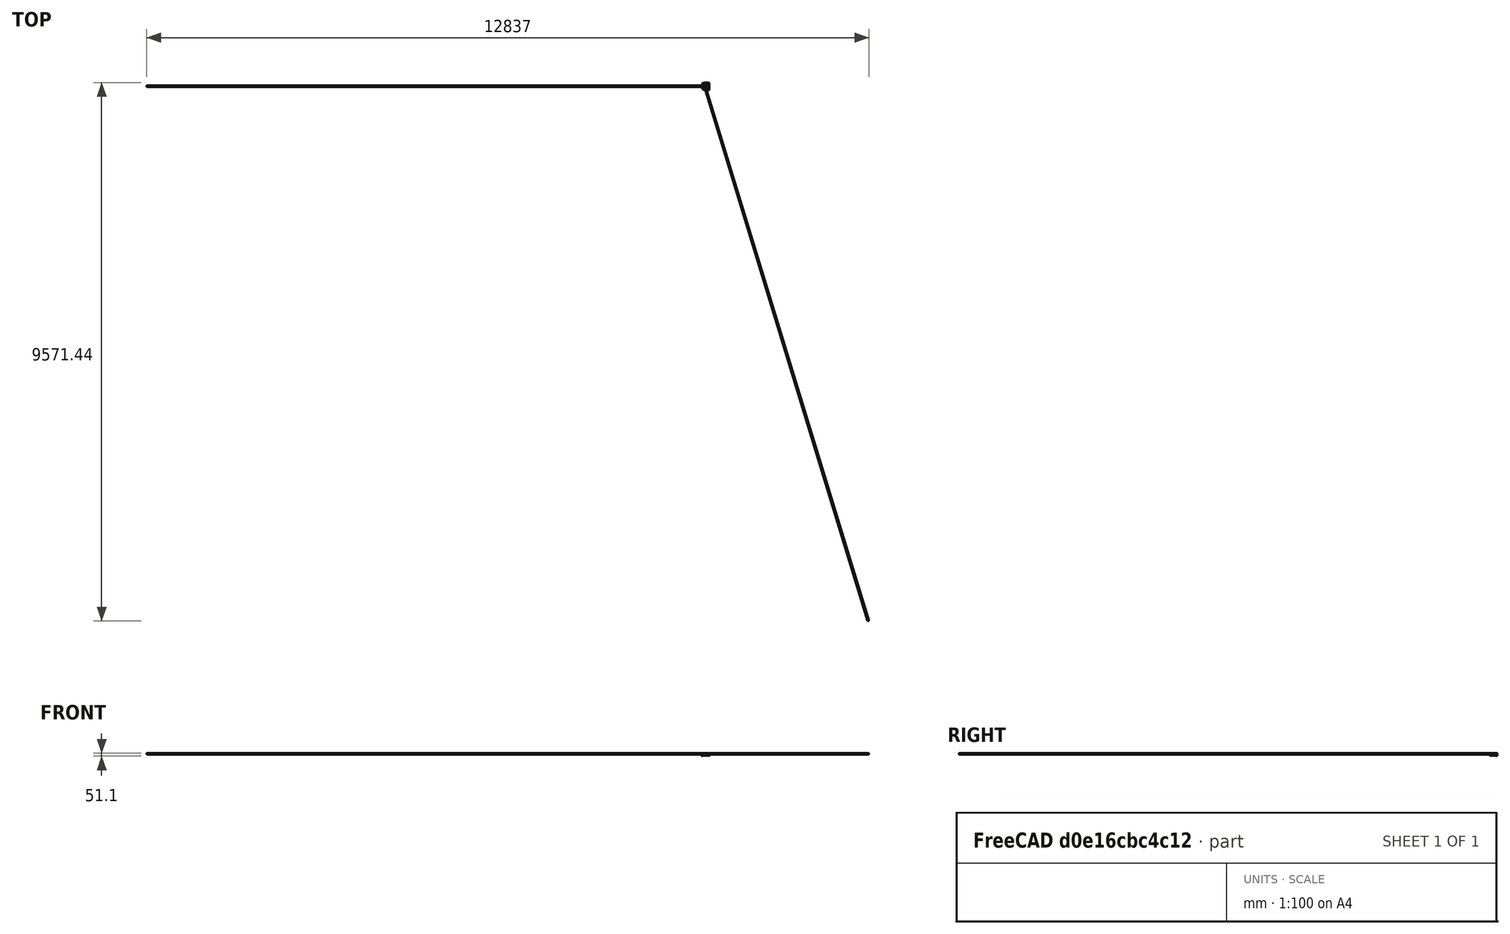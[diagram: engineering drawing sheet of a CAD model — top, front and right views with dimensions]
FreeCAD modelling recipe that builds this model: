
FCSTD DOCUMENT  (FreeCAD 0.16R)
Label: chainguard25TRearRev4
License: All rights reserved
LicenseURL: http://en.wikipedia.org/wiki/All_rights_reserved
objects: Sketcher::SketchObject×12, PartDesign::Pocket×6, PartDesign::Pad×5, PartDesign::Fillet×5, Part::FeaturePython×4, Mesh::Feature×4
note: 43 computed .brp shape members not serialized (recipe doc carries the construction recipe); baked Part::Feature solids carry a one-line shape summary decoded from their .brp

FEATURE [Sketcher::SketchObject] Sketch001
  sketch-geometry (7):
    g0: LineSegment StartX=60 StartY=64 StartZ=0 EndX=0 EndY=64 EndZ=0
    g1: LineSegment StartX=60 StartY=-64 StartZ=0 EndX=0 EndY=-64 EndZ=0
    g2: ArcOfCircle CenterX=8.21903e-05 CenterY=0 CenterZ=0 NormalX=0 NormalY=0 NormalZ=1 Radius=64 StartAngle=1.5708 EndAngle=4.71239
    g3: Circle CenterX=0 CenterY=0 CenterZ=0 NormalX=0 NormalY=0 NormalZ=1 Radius=45
    g4: ArcOfCircle CenterX=60 CenterY=51 CenterZ=0 NormalX=0 NormalY=0 NormalZ=1 Radius=13 StartAngle=0 EndAngle=1.5708
    g5: ArcOfCircle CenterX=60 CenterY=-51 CenterZ=0 NormalX=0 NormalY=0 NormalZ=1 Radius=13 StartAngle=4.71239 EndAngle=6.28319
    g6: LineSegment StartX=73 StartY=51 StartZ=0 EndX=73 EndY=-51 EndZ=0
  constraints (23):
    c: Horizontal(g0)
    c: Horizontal(g1)
    c: Coincident(g2,g1)
    c: Coincident(g0,g2)
    c: DistanceX(g1,g0) = 0
    c: Equal(g0,g1)
    c: DistanceY(g1,g0) = 128
    c: Radius(g2) = 64
    c: Symmetric(g1,g0,g-1)
    c: Radius(g3) = 45
    c: Coincident(g3,g-1)
    c: PointOnObject(g4,g0)
    c: Radius(g4) = 13
    c: DistanceX(g0,g0) = 60
    c: Equal(g5,g4)
    c: Vertical(g6)
    c: DistanceX(g-1,g6) = 73
    c: Symmetric(g6,g6,g-1)
    c: DistanceY(g6,g6) = 102
    c: Coincident(g4,g6)
    c: Coincident(g5,g6)
    c: Coincident(g1,g5)
    c: Coincident(g0,g4)
FEATURE [PartDesign::Pad] Pad  label="Faceplate"
  Length = 1.12
  Length2 = 100
  Reversed = true
  Sketch = -> Sketch001
  Type = 0
FEATURE [Sketcher::SketchObject] Sketch002
  sketch-geometry (8):
    g0: LineSegment StartX=60 StartY=64 StartZ=0 EndX=0 EndY=64 EndZ=0
    g1: LineSegment StartX=60 StartY=-64 StartZ=0 EndX=0 EndY=-64 EndZ=0
    g2: ArcOfCircle CenterX=6.44712e-05 CenterY=0 CenterZ=0 NormalX=0 NormalY=0 NormalZ=1 Radius=64 StartAngle=1.5708 EndAngle=4.71239
    g3: LineSegment StartX=0 StartY=62 StartZ=0 EndX=60 EndY=62 EndZ=0
    g4: LineSegment StartX=0 StartY=-62 StartZ=0 EndX=60 EndY=-62 EndZ=0
    g5: LineSegment StartX=60 StartY=64 StartZ=0 EndX=60 EndY=62 EndZ=0
    g6: LineSegment StartX=60 StartY=-62 StartZ=0 EndX=60 EndY=-64 EndZ=0
    g7: ArcOfCircle CenterX=1.45954e-05 CenterY=0 CenterZ=0 NormalX=0 NormalY=0 NormalZ=1 Radius=62 StartAngle=1.5708 EndAngle=4.71239
  constraints (25):
    c: Horizontal(g0)
    c: Horizontal(g1)
    c: Coincident(g2,g1)
    c: Coincident(g0,g2)
    c: DistanceX(g1,g0) = 0
    c: Equal(g0,g1)
    c: DistanceY(g1,g0) = 128
    c: Radius(g2) = 64
    c: Symmetric(g1,g0,g-1)
    c: Radius(g7) = 62
    c: Parallel(g0,g3)
    c: DistanceY(g3,g0) = 2
    c: DistanceY(g1,g4) = 2
    c: Parallel(g4,g1)
    c: DistanceX(g0,g3) = 0
    c: DistanceX(g4) = 0
    c: DistanceX(g0) = 60
    c: Equal(g3,g0)
    c: Equal(g4,g0)
    c: Coincident(g4,g6)
    c: Coincident(g6,g1)
    c: Coincident(g5,g3)
    c: Coincident(g5,g0)
    c: Coincident(g7,g3)
    c: Coincident(g7,g4)
FEATURE [PartDesign::Pad] Pad001  label="Connector"
  Length = 12
  Length2 = 100
  Sketch = -> Sketch002
  Type = 0
FEATURE [Sketcher::SketchObject] Sketch017
  sketch-geometry (5):
    g0: LineSegment [constr] StartX=-6 StartY=2 StartZ=0 EndX=-29.8283 EndY=79.9388 EndZ=0
    g1: LineSegment StartX=-7.74339 StartY=67.5577 StartZ=0 EndX=-41.2141 EndY=57.3247 EndZ=0
    g2: LineSegment StartX=-41.2141 StartY=57.3247 StartZ=0 EndX=-39.4598 EndY=51.5868 EndZ=0
    g3: LineSegment StartX=-39.4598 StartY=51.5868 StartZ=0 EndX=-5.98916 EndY=61.8199 EndZ=0
    g4: LineSegment StartX=-5.98916 StartY=61.8199 StartZ=0 EndX=-7.74339 EndY=67.5577 EndZ=0
  constraints (15):
    c: DistanceY(g-1,g0) = 2
    c: DistanceX(g-1,g0) = -6
    c: Angle(g0) = 1.8675
    c: Coincident(g1,g2)
    c: Coincident(g2,g3)
    c: Coincident(g3,g4)
    c: Coincident(g1,g4)
    c: Parallel(g2,g4)
    c: Parallel(g1,g3)
    c: Perpendicular(g2,g1)
    c: Distance(g4) = 6
    c: Distance(g1) = 35
    c: Symmetric(g3,g2,g0)
    c: Distance(g-1,g1) = 68
    c: Distance(g0) = 81.5
FEATURE [Sketcher::SketchObject] Sketch020
  sketch-geometry (4):
    g0: LineSegment StartX=67 StartY=35 StartZ=0 EndX=73 EndY=35 EndZ=0
    g1: LineSegment StartX=73 StartY=35 StartZ=0 EndX=73 EndY=-25 EndZ=0
    g2: LineSegment StartX=73 StartY=-25 StartZ=0 EndX=67 EndY=-25 EndZ=0
    g3: LineSegment StartX=67 StartY=-25 StartZ=0 EndX=67 EndY=35 EndZ=0
  constraints (12):
    c: Coincident(g0,g1)
    c: Coincident(g1,g2)
    c: Coincident(g2,g3)
    c: Coincident(g3,g0)
    c: Horizontal(g0)
    c: Horizontal(g2)
    c: Vertical(g1)
    c: Vertical(g3)
    c: DistanceX(g-1,g0) = 73
    c: DistanceX(g0,g0) = 6
    c: DistanceY(g-1,g0) = 35
    c: DistanceY(g1,g1) = 60
FEATURE [PartDesign::Pad] Pad004  label="SyncBoss"
  Length = 31
  Length2 = 100
  Sketch = -> Sketch020
  Type = 0
FEATURE [Sketcher::SketchObject] Sketch021
  ExternalGeometry = -> [Pad004]
  Placement = pos=(73,0,0) rot=(0.57735,0.57735,0.57735;2.0944rad)
  Support = -> Pad004 [Face2]
  sketch-geometry (1):
    g0: Circle CenterX=5 CenterY=31 CenterZ=0 NormalX=0 NormalY=0 NormalZ=1 Radius=11.2
  constraints (2):
    c: Symmetric(g-4,g-3,g0)
    c: Radius(g0) = 11.2
FEATURE [PartDesign::Pocket] Pocket  label="SyncHole"
  Length = 5
  Sketch = -> Sketch021
  Type = 1
FEATURE [PartDesign::Pad] Pad005  label="STBoss"
  Length = 32
  Length2 = 1
  Sketch = -> Sketch017
  Type = 4
FEATURE [Sketcher::SketchObject] Sketch022
  ExternalGeometry = -> [Pad005]
  Placement = pos=(-19.5508,63.9478,0) rot=(-0.105093,0.703191,0.703191;3.35101rad)
  Support = -> Pad005 [Face1]
  sketch-geometry (1):
    g0: Circle CenterX=5.15309 CenterY=32 CenterZ=0 NormalX=0 NormalY=0 NormalZ=1 Radius=11.2
  constraints (2):
    c: Symmetric(g-4,g-3,g0)
    c: Radius(g0) = 11.2
FEATURE [PartDesign::Pocket] Pocket006  label="SThole"
  Length = 5
  Sketch = -> Sketch022
  Type = 1
FEATURE [Sketcher::SketchObject] Sketch023
  Placement = pos=(-19.5508,63.9478,0) rot=(-0.105093,0.703191,0.703191;3.35101rad)
  Support = -> Pocket006 [Face1]
  sketch-geometry (3):
    g0: LineSegment StartX=31.754 StartY=21.6568 StartZ=0 EndX=10.7035 EndY=-1 EndZ=0
    g1: LineSegment StartX=10.7035 StartY=-1 StartZ=0 EndX=40.8501 EndY=-7.90189 EndZ=0
    g2: LineSegment StartX=40.8501 StartY=-7.90189 StartZ=0 EndX=31.754 EndY=21.6568 EndZ=0
  constraints (9):
    c: Coincident(g0,g1)
    c: Coincident(g1,g2)
    c: Coincident(g0,g2)
    c: Equal(g0,g2)
    c: Equal(g2,g1)
    c: DistanceY(g0,g-1) = 1
    c: Angle(g1) = -0.225065
    c: Distance(g2) = 30.9266
    c: DistanceX(g-1,g0) = 10.7035
FEATURE [PartDesign::Pocket] Pocket007  label="STbevel1"
  Length = 6
  Sketch = -> Sketch023
  Type = 0
FEATURE [Sketcher::SketchObject] Sketch024
  sketch-geometry (6):
    g0: ArcOfCircle CenterX=0 CenterY=0 CenterZ=0 NormalX=0 NormalY=0 NormalZ=1 Radius=48 StartAngle=1.34179 EndAngle=4.9414
    g1: Circle CenterX=0 CenterY=0 CenterZ=0 NormalX=0 NormalY=0 NormalZ=1 Radius=45
    g2: LineSegment StartX=10.8966 StartY=46.7468 StartZ=0 EndX=65 EndY=35.4994 EndZ=0
    g3: LineSegment StartX=65 StartY=35.5006 StartZ=0 EndX=65 EndY=-35.4994 EndZ=0
    g4: LineSegment StartX=65 StartY=-35.4994 StartZ=0 EndX=10.8966 EndY=-46.7468 EndZ=0
    g5: LineSegment StartX=65 StartY=35.5 StartZ=0 EndX=65 EndY=-35.5 EndZ=0
  constraints (14):
    c: Coincident(g0,g-1)
    c: Radius(g0) = 48
    c: Coincident(g1,g-1)
    c: Radius(g1) = 45
    c: Coincident(g3,g4)
    c: Coincident(g0,g2)
    c: Distance(g3) = 71
    c: DistanceX(g-1,g2) = 65
    c: Equal(g4,g2)
    c: Vertical(g3)
    c: Symmetric(g2,g3,g-1)
    c: Distance(g2) = 55.2601
    c: DistanceY(g-1,g0) = 46.7468
    c: DistanceX(g0) = 10.8966
FEATURE [Sketcher::SketchObject] Sketch026
  sketch-geometry (4):
    g0: LineSegment StartX=0 StartY=47.5 StartZ=0 EndX=73 EndY=35 EndZ=0
    g1: LineSegment StartX=73 StartY=35 StartZ=0 EndX=73 EndY=-35 EndZ=0
    g2: LineSegment StartX=73 StartY=-35 StartZ=0 EndX=0 EndY=-47.5 EndZ=0
    g3: LineSegment StartX=0 StartY=-47.5 StartZ=0 EndX=0 EndY=47.5 EndZ=0
  constraints (11):
    c: Coincident(g0,g1)
    c: Coincident(g1,g2)
    c: Coincident(g2,g3)
    c: Coincident(g3,g0)
    c: Symmetric(g2,g0,g-1)
    c: Symmetric(g2,g0,g-1)
    c: Equal(g0,g2)
    c: Vertical(g1)
    c: DistanceY(g1,g1) = 70
    c: DistanceY(g3,g3) = 95
    c: DistanceX(g-1,g0) = 73
FEATURE [PartDesign::Pad] Pad007  label="FieldStiffener"
  Length = 1
  Length2 = 100
  Sketch = -> Sketch026
  Type = 0
FEATURE [Sketcher::SketchObject] Sketch028
  ExternalGeometry = -> [Pocket]
  Placement = pos=(0,0,31) rot=(0,0,1;0rad)
  Support = -> Pocket [Face5]
  sketch-geometry (2):
    g0: Circle CenterX=70 CenterY=19 CenterZ=0 NormalX=0 NormalY=0 NormalZ=1 Radius=1.4
    g1: Circle CenterX=70 CenterY=-9 CenterZ=0 NormalX=0 NormalY=0 NormalZ=1 Radius=1.4
  constraints (6):
    c: DistanceY(g-4,g0) = 2.8
    c: DistanceX(g0,g-4) = 3
    c: DistanceX(g1,g-6) = 3
    c: DistanceY(g1,g-5) = 2.8
    c: Equal(g1,g0)
    c: Radius(g1) = 1.4
FEATURE [PartDesign::Pocket] Pocket010  label="SyncScrewHoles"
  Length = 15
  Sketch = -> Sketch028
  Type = 0
FEATURE [Sketcher::SketchObject] Sketch029
  ExternalGeometry = -> [Pocket010]
  Placement = pos=(73,0,0) rot=(0.57735,0.57735,0.57735;2.0944rad)
  Support = -> Pocket010 [Face3]
  sketch-geometry (6):
    g0: LineSegment StartX=35 StartY=3 StartZ=0 EndX=22.5 EndY=32 EndZ=0
    g1: LineSegment StartX=22.5 StartY=32 StartZ=0 EndX=-12.5 EndY=32 EndZ=0
    g2: LineSegment StartX=-12.5 StartY=32 StartZ=0 EndX=-25 EndY=3 EndZ=0
    g3: LineSegment StartX=-25 StartY=3 StartZ=0 EndX=-28.2949 EndY=52.1665 EndZ=0
    g4: LineSegment StartX=-28.2949 StartY=52.1665 StartZ=0 EndX=43.0613 EndY=52.1665 EndZ=0
    g5: LineSegment StartX=43.0613 StartY=52.1665 StartZ=0 EndX=35 EndY=3 EndZ=0
  constraints (18):
    c: Coincident(g0,g1)
    c: Horizontal(g1)
    c: Coincident(g1,g2)
    c: Coincident(g2,g3)
    c: Coincident(g3,g4)
    c: Horizontal(g4)
    c: Coincident(g4,g5)
    c: Coincident(g0,g5)
    c: DistanceX(g-4,g0) = 6.3
    c: DistanceX(g1,g-4) = 6.3
    c: DistanceX(g-3,g0) = 0
    c: DistanceX(g2,g-6) = 0
    c: DistanceX(g4,g4) = 71.3562
    c: Distance(g3) = 49.2768
    c: Distance(g5) = 49.823
    c: DistanceY(g-4,g1) = 1
    c: DistanceY(g-6,g2) = 3
    c: DistanceY(g-3,g0) = 3
FEATURE [PartDesign::Pocket] Pocket011  label="SyncBigBevel"
  Length = 5
  Sketch = -> Sketch029
  Type = 1
FEATURE [PartDesign::Fillet] Fillet  label="SyncFillets"
  Base = -> Pocket011 [Edge13,Edge14,Edge15,Edge3,Edge9,Edge21,Edge19,Edge22]
  Radius = 1
FEATURE [Sketcher::SketchObject] Sketch030
  ExternalGeometry = -> [Pocket007]
  Placement = pos=(0,0,32) rot=(0,0,1;0rad)
  Support = -> Pocket007 [Face5]
  sketch-geometry (2):
    g0: Circle CenterX=-37.0422 CenterY=55.5316 CenterZ=0 NormalX=0 NormalY=0 NormalZ=1 Radius=1.4
    g1: Circle CenterX=-10.2466 CenterY=63.6553 CenterZ=0 NormalX=0 NormalY=0 NormalZ=1 Radius=1.4
  constraints (6):
    c: Equal(g0,g1)
    c: Radius(g0) = 1.4
    c: Distance(g1,g-6) = 3
    c: Distance(g0,g1) = 28
    c: Distance(g0,g-8) = 4.08
    c: Distance(g1,g-6) = 4.08
FEATURE [PartDesign::Pocket] Pocket012
  Length = 15
  Sketch = -> Sketch030
  Type = 0
FEATURE [PartDesign::Fillet] Fillet001  label="STfillets"
  Base = -> Pocket012 [Edge23,Edge7,Edge8,Edge20,Edge12,Edge13,Edge14,Edge3,Edge2,Edge10,Edge11,Edge9,Edge1]
  Radius = 2
FEATURE [PartDesign::Fillet] Fillet002
  Base = -> Pad001 [Edge24,Edge13]
  Radius = 10
FEATURE [PartDesign::Fillet] Fillet003
  Base = -> Pad [Edge4,Edge7,Edge10,Edge13,Edge16,Edge18,Edge21]
  Radius = 0.6
FEATURE [PartDesign::Fillet] Fillet004
  Base = -> Fillet002 [Edge17]
  Radius = 1
FEATURE [Part::FeaturePython] refine  label="refine_Fillet004"  # WARN: FeaturePython — macro-defined, semantics opaque (R4)
  Base = -> Fillet004
FEATURE [Part::FeaturePython] refine001  label="refine_Fillet003"  # WARN: FeaturePython — macro-defined, semantics opaque (R4)
  Base = -> Fillet003
FEATURE [Part::FeaturePython] refine002  label="refine_STfillets"  # WARN: FeaturePython — macro-defined, semantics opaque (R4)
  Base = -> Fillet001
FEATURE [Part::FeaturePython] refine003  label="refine_SyncFillets"  # WARN: FeaturePython — macro-defined, semantics opaque (R4)
  Base = -> Fillet
FEATURE [Mesh::Feature] Mesh  label="refine_Fillet004 (Meshed)"
FEATURE [Mesh::Feature] Mesh001  label="refine_Fillet003 (Meshed)"
FEATURE [Mesh::Feature] Mesh002  label="refine_STfillets (Meshed)"
FEATURE [Mesh::Feature] Mesh003  label="refine_SyncFillets (Meshed)"
